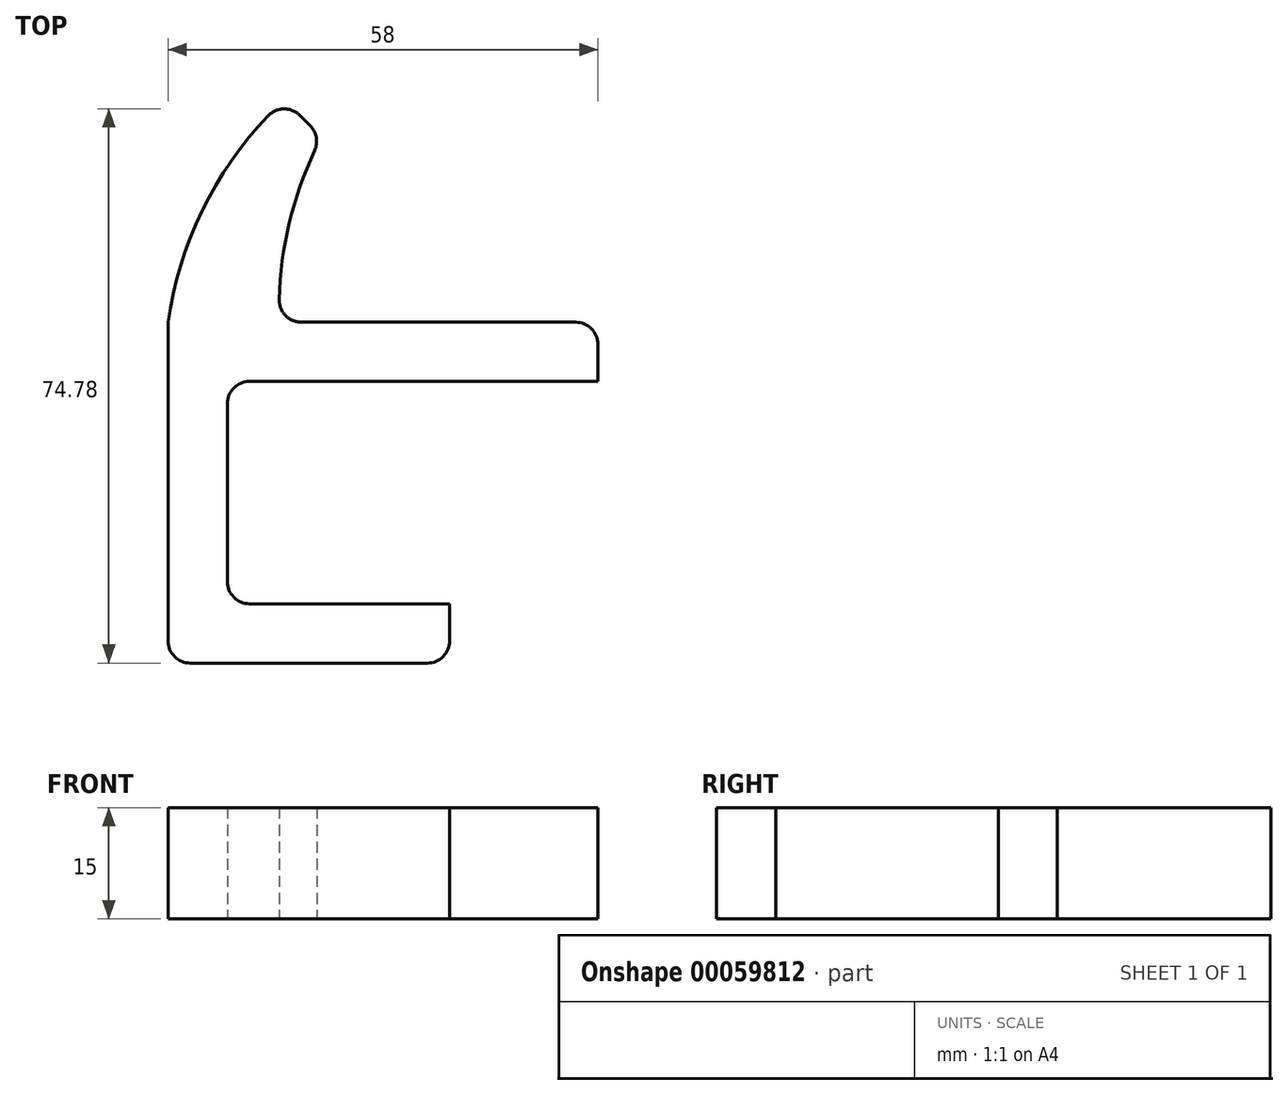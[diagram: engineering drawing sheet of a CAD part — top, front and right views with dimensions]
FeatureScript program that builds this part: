
annotation { "Feature Type Name" : "Feature", "Feature Type Description" : "" }
export const myFeature = defineFeature(function(context is Context, id is Id, definition is map)
    precondition{}
    {
        {
            var Q0;
            Q0=qCreatedBy(makeId("Top.planeOp"),FACE);
            var sketch = newSketch(context, id + "F0", { "sketchPlane" : qUnion([Q0])});
            skLineSegment(sketch, "E0", {"start": v(3, 0) * mm, "end": v(35, 0) * mm});
            skLineSegment(sketch, "E1", {"start": v(38, 3) * mm, "end": v(38, 8) * mm});
            skLineSegment(sketch, "E2", {"start": v(38, 8) * mm, "end": v(11, 8) * mm});
            skLineSegment(sketch, "E3", {"start": v(8, 11) * mm, "end": v(8, 35) * mm});
            skLineSegment(sketch, "E4", {"start": v(11, 38) * mm, "end": v(58, 38) * mm});
            skLineSegment(sketch, "E5", {"start": v(58, 38) * mm, "end": v(58, 43) * mm});
            skLineSegment(sketch, "E6", {"start": v(55, 46) * mm, "end": v(18, 46) * mm});
            skLineSegment(sketch, "E7", {"start": v(0, 3) * mm, "end": v(0, 46) * mm});
            skArc(sketch, "E8", {"start": v(0, 46) * mm, "mid": v(4.57, 60.99) * mm, "end": v(13.5, 73.85) * mm});
            skArc(sketch, "E9", {"start": v(15, 49.08) * mm, "mid": v(16.34, 59.35) * mm, "end": v(19.77, 69.13) * mm});
            skLineSegment(sketch, "E10", {"start": v(19.17, 72.52) * mm, "end": v(17.8, 73.9) * mm});
            skPoint(sketch, "E11", {"position": v(15.7, 76) * mm});
            skPoint(sketch, "E12.visualSharp", {"position": v(0, 0) * mm});
            skArc(sketch, "E12.filletArc", {"start": v(0, 3) * mm, "mid": v(0.88, 0.88) * mm, "end": v(3, 0) * mm});
            skPoint(sketch, "E13.visualSharp", {"position": v(8, 8) * mm});
            skArc(sketch, "E13.filletArc", {"start": v(8, 11) * mm, "mid": v(8.88, 8.88) * mm, "end": v(11, 8) * mm});
            skPoint(sketch, "E14.visualSharp", {"position": v(8, 38) * mm});
            skArc(sketch, "E14.filletArc", {"start": v(11, 38) * mm, "mid": v(8.88, 37.12) * mm, "end": v(8, 35) * mm});
            skPoint(sketch, "E15.visualSharp", {"position": v(15, 46) * mm});
            skArc(sketch, "E15.filletArc", {"start": v(15, 49.08) * mm, "mid": v(15.84, 46.9) * mm, "end": v(18, 46) * mm});
            skArc(sketch, "E16.filletArc", {"start": v(17.8, 73.9) * mm, "mid": v(15.64, 74.78) * mm, "end": v(13.5, 73.85) * mm});
            skPoint(sketch, "E17.visualSharp", {"position": v(20.7, 71) * mm});
            skArc(sketch, "E17.filletArc", {"start": v(19.77, 69.13) * mm, "mid": v(20, 70.92) * mm, "end": v(19.17, 72.52) * mm});
            skPoint(sketch, "E18.visualSharp", {"position": v(38, 0) * mm});
            skArc(sketch, "E18.filletArc", {"start": v(35, 0) * mm, "mid": v(37.12, 0.88) * mm, "end": v(38, 3) * mm});
            skPoint(sketch, "E19.visualSharp", {"position": v(58, 46) * mm});
            skArc(sketch, "E19.filletArc", {"start": v(58, 43) * mm, "mid": v(57.12, 45.12) * mm, "end": v(55, 46) * mm});
            skSolve(sketch);
        }
        {
            var Q0;
            Q0=makeQuery(id+"F0.imprint","IMPRINT",FACE,{"disambiguationData":[TD([[makeQuery(id+"F0.imprint","IMPRINT",EDGE,{"derivedFrom":sQuery(id+"F0.wireOp",EDGE,"E0")}),1.0]])]});
            extrude(context, id + "F1", {"entities" : qUnion([Q0]), "depth" : 15 * mm});
        }
    });
